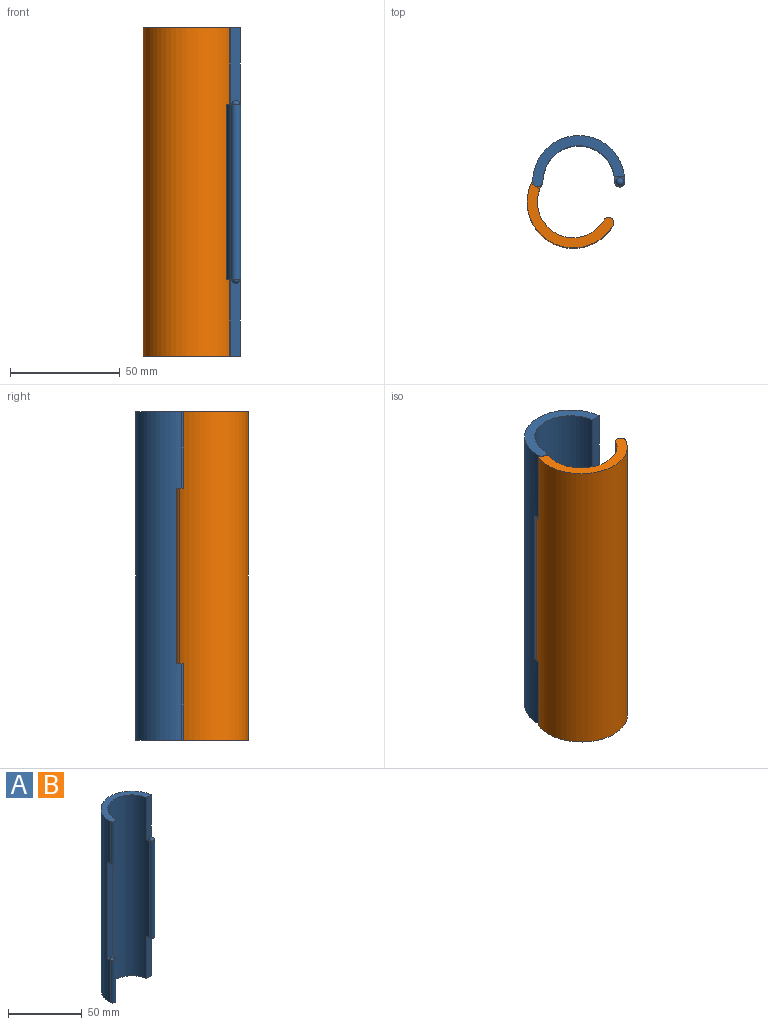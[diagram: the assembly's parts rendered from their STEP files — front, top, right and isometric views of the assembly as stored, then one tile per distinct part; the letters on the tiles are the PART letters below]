
ASSEMBLY  parts=2 mates=1
PART A: 18 faces, bbox 42x23.3x150 mm
  f0: cylinder r=21mm len=150mm, axis (0,0,-1), area 9535.2mm2, adj f2,f3,f4,f5,f6,f7,f8,f9
  f1: cylinder r=16.35mm len=150mm, axis (0,0,-1), area 7343.5mm2, adj f2,f3,f4,f5,f6,f7,f8,f9
  f2: cylinder r=2.32mm len=80mm, axis (0,0,-1), area 584.3mm2, adj f0,f1,f10,f12
  f3: cylinder r=2.32mm len=35mm, axis (0,0,-1), area 255.6mm2, adj f0,f1,f5,f7
  f4: cylinder r=2.32mm len=35mm, axis (0,0,-1), area 255.6mm2, adj f0,f1,f6,f8
  f5: plane 41.86x23.33mm, normal (0,0,1), area 270.1mm2, adj f0,f1,f3,f13
  f6: plane 41.86x23.33mm, normal (0,0,-1), area 270.1mm2, adj f0,f1,f4,f11
  f7: plane 4.83x4.73mm, normal (0,0,-1), area 10.1mm2, adj f0,f1,f3,f9,f17
  f8: plane 4.83x4.73mm, normal (0,0,1), area 10.1mm2, adj f0,f1,f4,f9,f16
  f9: plane 80x4.69mm, normal (0,-1,0), area 375.2mm2, adj f0,f1,f7,f8
  f10: plane 4.83x4.73mm, normal (0,0,-1), area 10.1mm2, adj f0,f1,f2,f11,f15
  f11: plane 35x4.69mm, normal (0,-1,0), area 164.1mm2, adj f0,f1,f6,f10
  f12: plane 4.83x4.73mm, normal (0,0,1), area 10.1mm2, adj f0,f1,f2,f13,f14
  f13: plane 35x4.69mm, normal (0,-1,0), area 164.1mm2, adj f0,f1,f5,f12
  f14: sphere r=1.75mm, area 19.2mm2, adj f12
  f15: sphere r=1.75mm, area 19.2mm2, adj f10
  f16: sphere r=1.75mm, area 19.2mm2, adj f8
  f17: sphere r=1.75mm, area 19.2mm2, adj f7
PART B: same geometry as A
PLACE A t=(-101.19,42.74,-12.89)mm
PLACE B rot(axis=(0,0,1),150deg) t=(-103.69,33.4,-12.89)mm
MATE ball B.f2 <-> A.f3  axis (0,0,1) through (-119.86,42.74,102.11)mm
